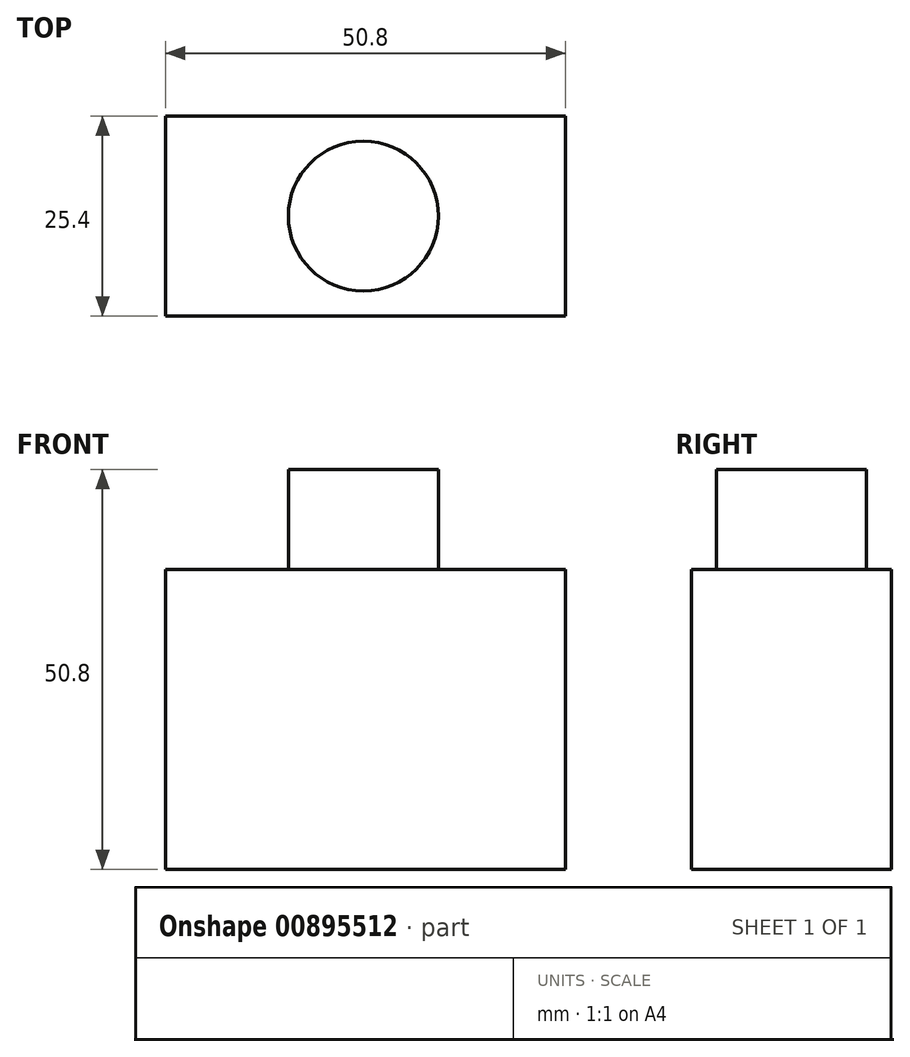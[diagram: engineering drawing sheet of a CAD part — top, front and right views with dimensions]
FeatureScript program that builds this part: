
annotation { "Feature Type Name" : "Feature", "Feature Type Description" : "" }
export const myFeature = defineFeature(function(context is Context, id is Id, definition is map)
    precondition{}
    {
        {
            var Q0;
            Q0=qCreatedBy(makeId("Front.planeOp"),FACE);
            var sketch = newSketch(context, id + "F0", { "sketchPlane" : qUnion([Q0])});
            skLineSegment(sketch, "E0.bottom", {"start": v(0, 0) * mm, "end": v(-50.8, 0) * mm});
            skLineSegment(sketch, "E0.top", {"start": v(0, 38.1) * mm, "end": v(-50.8, 38.1) * mm});
            skLineSegment(sketch, "E0.left", {"start": v(0, 0) * mm, "end": v(0, 38.1) * mm});
            skLineSegment(sketch, "E0.right", {"start": v(-50.8, 0) * mm, "end": v(-50.8, 38.1) * mm});
            skSolve(sketch);
        }
        {
            var Q0;
            Q0=makeQuery(id+"F0.imprint","IMPRINT",FACE,{"disambiguationData":[TD([[makeQuery(id+"F0.imprint","IMPRINT",EDGE,{"derivedFrom":sQuery(id+"F0.wireOp",EDGE,"E0.bottom")}),-1.0]])]});
            extrude(context, id + "F1", {"entities" : qUnion([Q0]), "endBound" : BoundingType.SYMMETRIC, "depth" : 25.4 * mm, "offsetDistance" : 25.4 * mm});
        }
        {
            var Q0;
            Q0=makeQuery(id+"F1.opExtrude","SWEPT_FACE",FACE,{"disambiguationData":[OSD([sQuery(id+"F0.wireOp",EDGE,"E0.top")])]});
            var sketch = newSketch(context, id + "F2", { "sketchPlane" : qUnion([Q0])});
            skCircle(sketch, "E1", {"center": v(-25.68, 0) * mm, "radius": 9.53 * mm});
            skSolve(sketch);
        }
        {
            var Q0;
            Q0=makeQuery(id+"F2.imprint","IMPRINT",FACE,{"disambiguationData":[TD([[makeQuery(id+"F2.imprint","IMPRINT",EDGE,{"derivedFrom":sQuery(id+"F2.wireOp",EDGE,"E1")}),1.0]])]});
            extrude(context, id + "F3", {"entities" : qUnion([Q0]), "operationType" : NewBodyOperationType.ADD, "depth" : 12.7 * mm, "offsetDistance" : 25.4 * mm});
        }
    });
